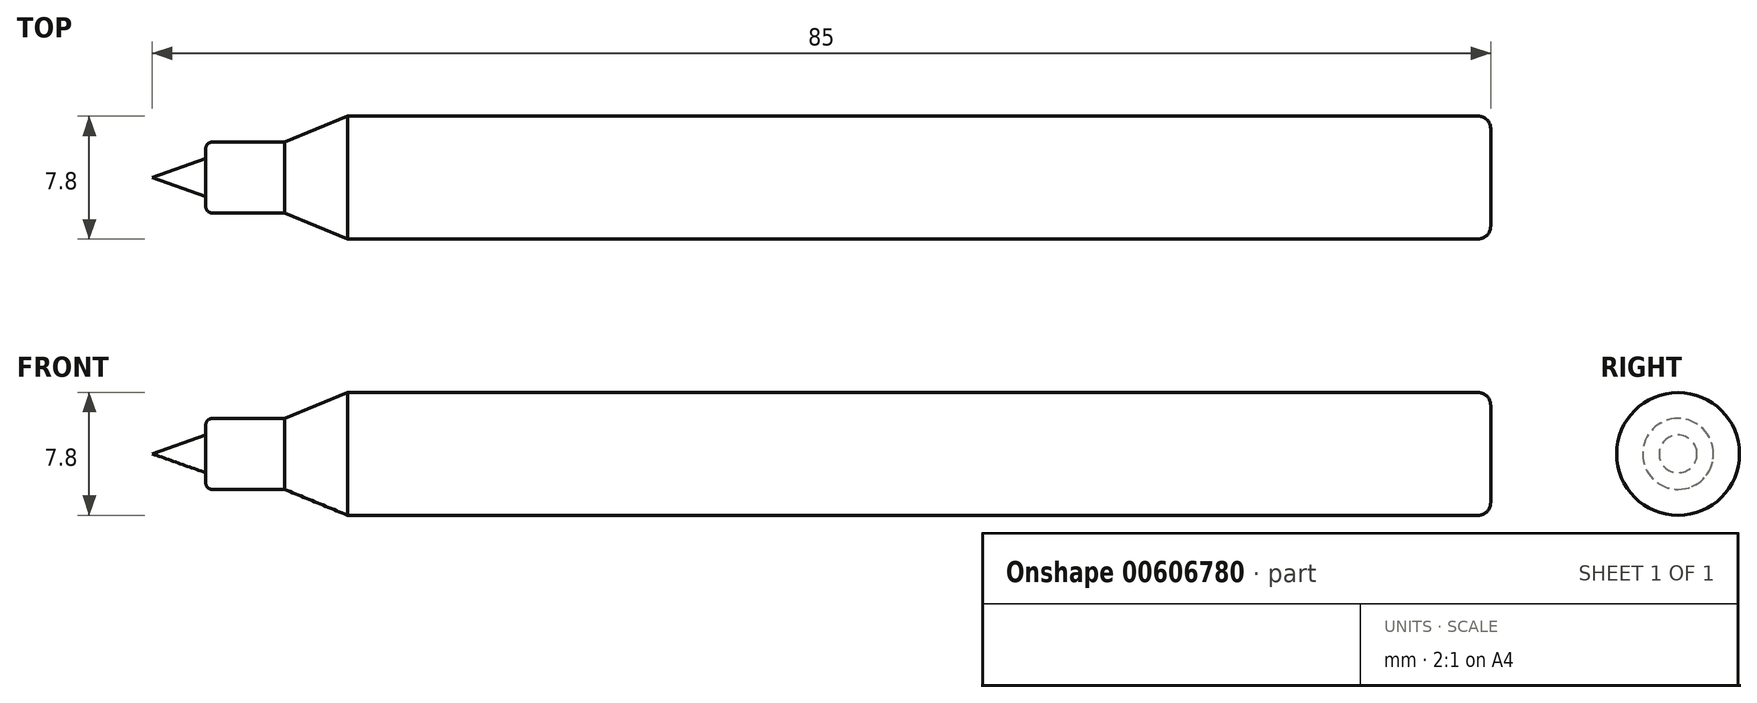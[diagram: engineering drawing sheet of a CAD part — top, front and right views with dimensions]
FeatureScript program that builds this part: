
annotation { "Feature Type Name" : "Feature", "Feature Type Description" : "" }
export const myFeature = defineFeature(function(context is Context, id is Id, definition is map)
    precondition{}
    {
        {
            var Q0;
            Q0=qCreatedBy(makeId("Top.planeOp"),FACE);
            var sketch = newSketch(context, id + "F0", { "sketchPlane" : qUnion([Q0])});
            skLineSegment(sketch, "E0.bottom", {"start": v(-16.11, 14.8) * mm, "end": v(68.89, 14.8) * mm});
            skLineSegment(sketch, "E0.top", {"start": v(-16.11, 7) * mm, "end": v(68.89, 7) * mm});
            skLineSegment(sketch, "E0.left", {"start": v(-16.11, 14.8) * mm, "end": v(-16.11, 7) * mm});
            skLineSegment(sketch, "E0.right", {"start": v(68.89, 14.8) * mm, "end": v(68.89, 7) * mm});
            skPoint(sketch, "E1", {"position": v(-3.71, 14.8) * mm});
            skPoint(sketch, "E2", {"position": v(-3.71, 7) * mm});
            skPoint(sketch, "E3", {"position": v(-7.71, 14.8) * mm});
            skPoint(sketch, "E4", {"position": v(-7.71, 7) * mm});
            skPoint(sketch, "E5", {"position": v(-12.71, 14.8) * mm});
            skPoint(sketch, "E6", {"position": v(-12.71, 7) * mm});
            skLineSegment(sketch, "E7.bottom", {"start": v(-16.11, 13.14) * mm, "end": v(-7.71, 13.14) * mm});
            skLineSegment(sketch, "E7.top", {"start": v(-16.11, 8.64) * mm, "end": v(-7.71, 8.64) * mm});
            skLineSegment(sketch, "E7.left", {"start": v(-16.11, 13.14) * mm, "end": v(-16.11, 8.64) * mm});
            skLineSegment(sketch, "E7.right", {"start": v(-7.71, 13.14) * mm, "end": v(-7.71, 8.64) * mm});
            skLineSegment(sketch, "E8", {"start": v(-7.71, 13.14) * mm, "end": v(-3.71, 14.8) * mm});
            skLineSegment(sketch, "E9", {"start": v(-7.71, 8.64) * mm, "end": v(-3.71, 7) * mm});
            skLineSegment(sketch, "E10", {"start": v(-12.71, 13.14) * mm, "end": v(-12.71, 8.64) * mm});
            skLineSegment(sketch, "E11", {"start": v(-12.71, 12.1) * mm, "end": v(-12.71, 9.7) * mm});
            skLineSegment(sketch, "E12", {"start": v(-12.71, 12.1) * mm, "end": v(-16.11, 10.9) * mm});
            skLineSegment(sketch, "E13", {"start": v(-16.11, 10.9) * mm, "end": v(-12.71, 9.7) * mm});
            skLineSegment(sketch, "E14", {"start": v(-3.71, 14.8) * mm, "end": v(-3.71, 7) * mm});
            skLineSegment(sketch, "E15", {"start": v(68.89, 10.9) * mm, "end": v(-16.11, 10.9) * mm});
            skSolve(sketch);
        }
        {
            var Q0;
            {var subQ0=sQuery(id+"F0.wireOp",EDGE,"E12");Q0=makeQuery(id+"F0.imprint","IMPRINT",FACE,{"disambiguationData":[TD([[makeQuery(id+"F0.imprint","IMPRINT",EDGE,{"derivedFrom":subQ0}),1.0]])]});}
            var Q1;
            {var subQ3=sQuery(id+"F0.wireOp",EDGE,"E15");var subQ5=sQuery(id+"F0.wireOp",EDGE,"E7.right");var subQ9=makeQuery(id+"F0.imprint","INTERSECT",VERTEX,{"derivedFrom":[subQ5,subQ3]});Q1=makeQuery(id+"F0.imprint","IMPRINT",FACE,{"disambiguationData":[TD([[makeQuery(id+"F0.imprint","IMPRINT",EDGE,{"disambiguationData":[TD([[subQ9,-1.0]])],"derivedFrom":subQ3}),-1.0]])]});}
            var Q2;
            {var subQ0=sQuery(id+"F0.wireOp",EDGE,"E8");Q2=makeQuery(id+"F0.imprint","IMPRINT",FACE,{"disambiguationData":[TD([[makeQuery(id+"F0.imprint","IMPRINT",EDGE,{"derivedFrom":subQ0}),-1.0]])]});}
            var Q3;
            {var subQ0=sQuery(id+"F0.wireOp",EDGE,"E0.right");var subQ1=sQuery(id+"F0.wireOp",EDGE,"E0.bottom");var subQ2=makeQuery(id+"F0.imprint","INTERSECT",VERTEX,{"derivedFrom":[subQ1,subQ0]});Q3=makeQuery(id+"F0.imprint","IMPRINT",FACE,{"disambiguationData":[TD([[makeQuery(id+"F0.imprint","IMPRINT",EDGE,{"disambiguationData":[TD([[subQ2,-1.0]])],"derivedFrom":subQ0}),-1.0]])]});}
            var Q4;
            Q4=sQuery(id+"F0.wireOp",EDGE,"E15");
            revolve(context, id + "F1", {"entities" : qUnion([Q0, Q1, Q2, Q3]), "axis" : qUnion([Q4]), "revolveType" : RevolveType.FULL});
        }
        {
            var Q0;
            Q0=makeQuery(id+"F1.opRevolve","SWEPT_EDGE",EDGE,{"disambiguationData":[OSD([sQuery(id+"F0.wireOp",EDGE,"E0.bottom"),sQuery(id+"F0.wireOp",EDGE,"E0.right")])]});
            fillet(context, id + "F2", {"entities" : qUnion([Q0]), "radius" : 0.8 * mm, "tangentPropagation" : true, "allowEdgeOverflow" : false});
        }
        {
            var Q0;
            Q0=makeQuery(id+"F1.opRevolve","SWEPT_EDGE",EDGE,{"disambiguationData":[OSD([sQuery(id+"F0.wireOp",EDGE,"E7.bottom"),sQuery(id+"F0.wireOp",EDGE,"E10")])]});
            fillet(context, id + "F3", {"entities" : qUnion([Q0]), "radius" : 0.4 * mm, "tangentPropagation" : true, "allowEdgeOverflow" : false});
        }
    });
